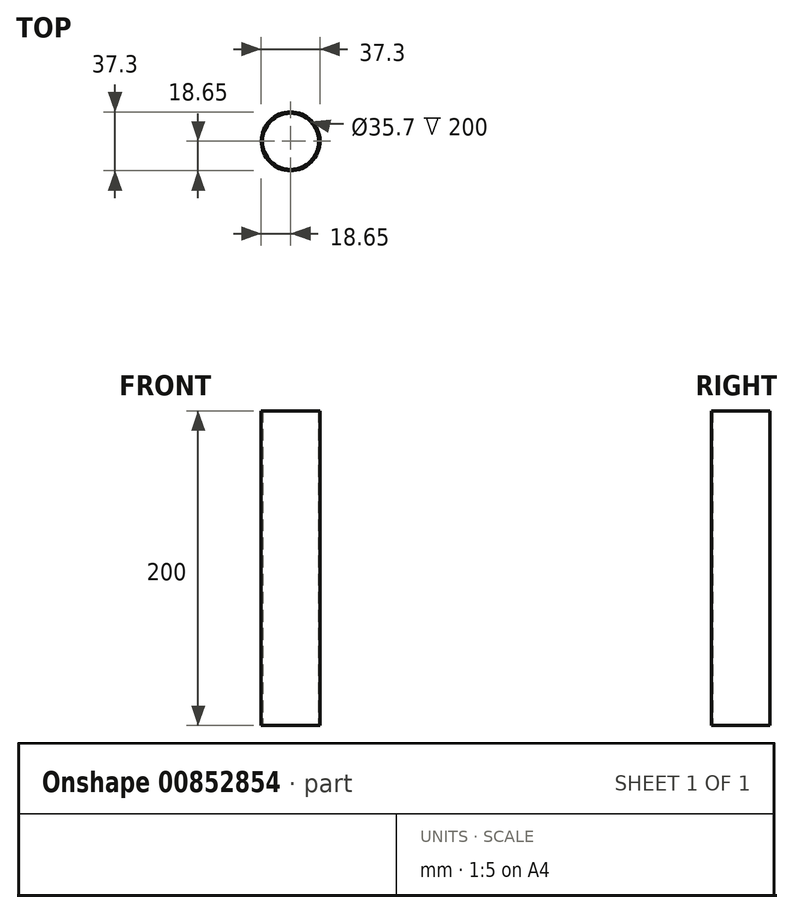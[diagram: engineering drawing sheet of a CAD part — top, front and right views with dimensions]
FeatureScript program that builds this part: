
annotation { "Feature Type Name" : "Feature", "Feature Type Description" : "" }
export const myFeature = defineFeature(function(context is Context, id is Id, definition is map)
    precondition{}
    {
        {
            var Q0;
            Q0=qCreatedBy(makeId("Top.planeOp"),FACE);
            var sketch = newSketch(context, id + "F0", { "sketchPlane" : qUnion([Q0])});
            skCircle(sketch, "E0", {"center": v(0, 0) * mm, "radius": 18.65 * mm});
            skCircle(sketch, "E1", {"center": v(0, 0) * mm, "radius": 17.85 * mm});
            skSolve(sketch);
        }
        {
            var Q0;
            Q0=makeQuery(id+"F0.imprint","IMPRINT",FACE,{"disambiguationData":[TD([[makeQuery(id+"F0.imprint","IMPRINT",EDGE,{"derivedFrom":sQuery(id+"F0.wireOp",EDGE,"E0")}),1.0]])]});
            extrude(context, id + "F1", {"entities" : qUnion([Q0]), "depth" : 200 * mm, "offsetDistance" : 25 * mm});
        }
    });
